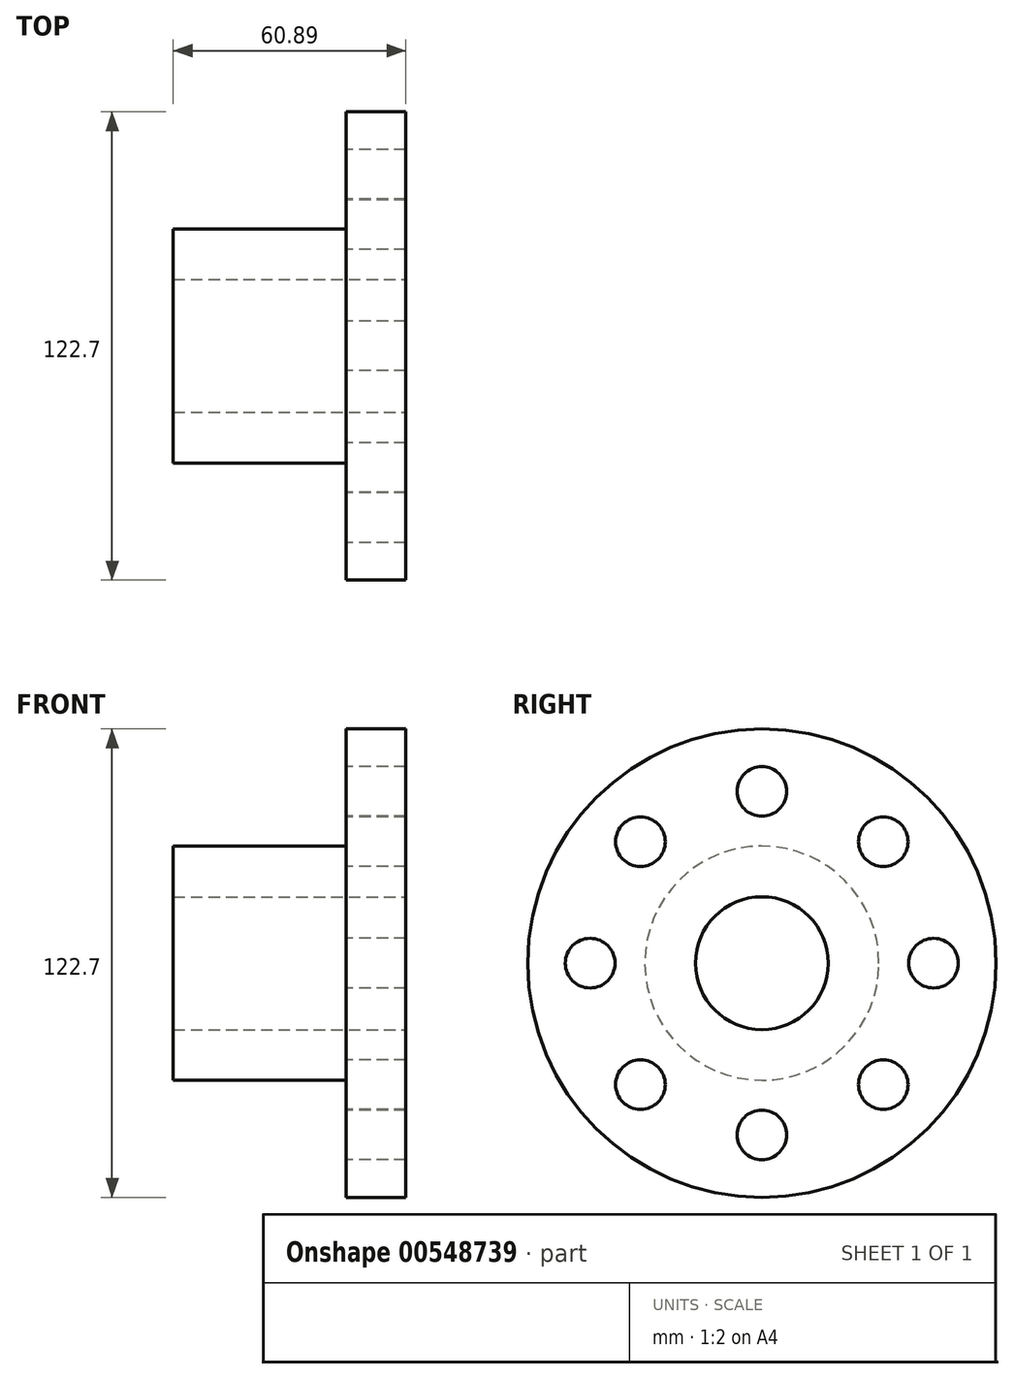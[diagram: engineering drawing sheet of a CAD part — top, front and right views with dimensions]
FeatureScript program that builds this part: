
annotation { "Feature Type Name" : "Feature", "Feature Type Description" : "" }
export const myFeature = defineFeature(function(context is Context, id is Id, definition is map)
    precondition{}
    {
        {
            var Q0;
            Q0=qCreatedBy(makeId("Front.planeOp"),FACE);
            var sketch = newSketch(context, id + "F0", { "sketchPlane" : qUnion([Q0])});
            skLineSegment(sketch, "E0", {"start": v(24.72, 17.4) * mm, "end": v(-36.17, 17.4) * mm});
            skLineSegment(sketch, "E1", {"start": v(-36.17, 17.4) * mm, "end": v(-36.17, 30.68) * mm});
            skLineSegment(sketch, "E2", {"start": v(-36.17, 30.68) * mm, "end": v(9.16, 30.68) * mm});
            skLineSegment(sketch, "E3", {"start": v(9.16, 30.68) * mm, "end": v(9.16, 61.35) * mm});
            skLineSegment(sketch, "E4", {"start": v(9.16, 61.35) * mm, "end": v(24.72, 61.35) * mm});
            skLineSegment(sketch, "E5", {"start": v(24.72, 61.35) * mm, "end": v(24.72, 17.4) * mm});
            skLineSegment(sketch, "E6", {"start": v(18.77, 0) * mm, "end": v(-51.74, 0) * mm, "construction": true});
            skSolve(sketch);
        }
        {
            var Q0;
            Q0=makeQuery(id+"F0.imprint","IMPRINT",FACE,{"disambiguationData":[TD([[makeQuery(id+"F0.imprint","IMPRINT",EDGE,{"derivedFrom":sQuery(id+"F0.wireOp",EDGE,"E0")}),-1.0]])]});
            var Q1;
            Q1=sQuery(id+"F0.wireOp",EDGE,"E6");
            var Q2;
            Q2=sQuery(id+"F0.wireOp",EDGE,"E6");
            revolve(context, id + "F1", {"entities" : qUnion([Q0]), "surfaceEntities" : qUnion([Q1]), "axis" : qUnion([Q2]), "revolveType" : RevolveType.FULL});
        }
        {
            var Q0;
            Q0=makeQuery(id+"F1.opRevolve","SWEPT_FACE",FACE,{"disambiguationData":[OSD([sQuery(id+"F0.wireOp",EDGE,"E3")])]});
            var sketch = newSketch(context, id + "F2", { "sketchPlane" : qUnion([Q0])});
            skLineSegment(sketch, "E7", {"start": v(0, 0) * mm, "end": v(0, 66.42) * mm, "construction": true});
            skCircle(sketch, "E8", {"center": v(0, 45) * mm, "radius": 6.5 * mm});
            skCircle(sketch, "E9.1.0", {"center": v(-31.82, 31.82) * mm, "radius": 6.5 * mm});
            skCircle(sketch, "E9.2.0", {"center": v(-45, 0) * mm, "radius": 6.5 * mm});
            skCircle(sketch, "E9.3.0", {"center": v(-31.82, -31.82) * mm, "radius": 6.5 * mm});
            skCircle(sketch, "E9.4.0", {"center": v(0, -45) * mm, "radius": 6.5 * mm});
            skCircle(sketch, "E9.5.0", {"center": v(31.82, -31.82) * mm, "radius": 6.5 * mm});
            skCircle(sketch, "E9.6.0", {"center": v(45, 0) * mm, "radius": 6.5 * mm});
            skCircle(sketch, "E9.7.0", {"center": v(31.82, 31.82) * mm, "radius": 6.5 * mm});
            skPoint(sketch, "E9.center", {"position": v(0, 0) * mm});
            skSolve(sketch);
        }
        {
            var Q0;
            Q0 = qSketchRegion(id + "F2", true);
            extrude(context, id + "F3", {"entities" : qUnion([Q0]), "operationType" : NewBodyOperationType.REMOVE, "endBound" : BoundingType.THROUGH_ALL, "oppositeDirection" : true, "depth" : 25 * mm, "offsetDistance" : 25 * mm});
        }
    });
